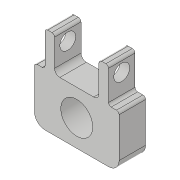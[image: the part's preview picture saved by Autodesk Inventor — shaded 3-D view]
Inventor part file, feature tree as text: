
AUTODESK INVENTOR PART (.ipt)
format: ipt  version: 2018.3 (Build 223284000, 284)  size: 151,552 bytes
history: native  units: in
note: dims shown in document units (in); Inventor stores cm internally (conversion verified against a paired STEP export)
features: extrude x4, fillet x3, sketch x3
ambient origin geometry x8: Origin, YZ Plane, XZ Plane, XY Plane, X Axis, Y Axis, Z Axis, Center Point
bodies: Solid1 (feature_tree)
feature tree (10):
  extrude  "Extrusion1"  Depth=0.225in
  extrude  "Extrusion2"  Depth=0.625in TaperAngle=0.0deg
  extrude  "Extrusion3"  Depth=2.0in TaperAngle=0.0deg
  fillet  "Fillet2"  Radius=0.375in
  fillet  "Fillet4"  Radius=0.3in
  fillet  "Fillet5"  Radius=0.5in
  extrude  "Extrusion4"  Depth=0.25in
  sketch  "Sketch1"  dims[d1=1.25in d4=0.225in]
  sketch  "Sketch2"  dims[d5=0.225in d7=0.625in d8=0.0in]
  sketch  "Sketch4"  dims[d10=0.755in d11=0.5in d12=0.0in d13=0.375in d15=0.3in d16=0.5in d17=0.0in d19=0.25in d21=0.825in d22=0.0625in d23=0.125in d24=0.625in d26=0.375in d27=1.0in d28=0.0in d29=0.25in d30=0.25in d31=1.0in d32=2.0in]
